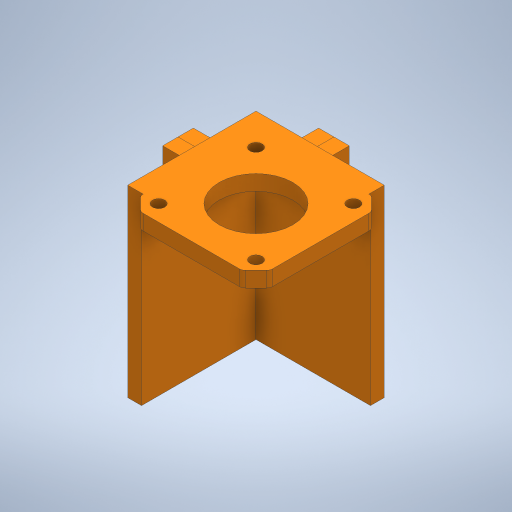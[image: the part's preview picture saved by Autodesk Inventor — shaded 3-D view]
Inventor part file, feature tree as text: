
AUTODESK INVENTOR PART (.ipt)
format: ipt  version: 2023 (Build 270158000, 158)  size: 452,608 bytes
history: native  units: mm
features: extrude x9, sketch x8, projected_geometry x4, other x3, fillet x1, reference x1
ambient origin geometry x8: Origin, YZ Plane, XZ Plane, XY Plane, X Axis, Y Axis, Z Axis, Center Point
bodies: Solid1 (feature_tree)
feature tree (26):
  extrude  "Extrusion1"  Depth=4.0mm
  extrude  "Extrusion3"  Depth=4.0mm
  extrude  "Extrusion4"  Depth=5.0mm TaperAngle=0.0deg
  extrude  "Extrusion9"  Depth=5.0mm
  extrude  "Extrusion7"  Depth=5.0mm TaperAngle=0.0deg
  extrude  "Extrusion10"  Depth=0.5mm
  extrude  "Extrusion11"  Depth=20.0mm TaperAngle=0.0deg
  extrude  "Extrusion12"  Depth=5.0mm
  fillet  "Fillet1"  Radius=4.5mm
  extrude  "Extrusion13"  Depth=0.5mm
  sketch  "Sketch1"  dims[d0=24.0mm d1=4.0mm]
  reference  "Reference1"
  sketch  "Sketch4"  dims[d2=4.0mm d3=4.0mm]
  projected_geometry  "Projected Loop1"
  sketch  "Sketch7"  dims[d4=4.0mm d5=5.0mm d6=0.0mm]
  sketch  "Sketch11"  dims[d11=5.0mm d12=5.0mm]
  sketch  "Sketch12"  dims[d15=40.0mm d16=0.0mm d17=5.0mm d18=0.0mm]
  sketch  "Sketch13"  dims[d35=0.5mm d36=0.5mm]
  sketch  "Sketch14"  dims[d37=35.0mm d38=0.0mm d52=20.0mm d53=0.0mm]
  projected_geometry  "Projected Loop2"
  sketch  "Sketch15"  dims[d54=5.0mm d55=5.0mm d56=4.5mm d57=0.5mm d58=20.0mm d59=0.0mm d60=10.0mm d61=10.0mm d62=5.0mm d63=5.0mm d64=20.0mm d65=10.0mm d66=20.0mm d67=0.0mm d68=10.0mm d69=10.0mm d70=20.0mm d71=10.0mm d72=5.0mm d73=5.0mm d74=40.0mm d75=0.0mm d76=5.0mm d77=8.0mm d78=8.0mm d79=5.0mm d80=5.0mm d81=20.0mm d82=20.0mm d83=0.0mm d84=0.0mm d85=20.0mm d86=0.0mm]
  projected_geometry  "Projected Loop3"
  projected_geometry  "Projected Loop4"
  other  "<userpath>\OneDrive\ClawdDrive\Objet3D\3DPrinter\inventor\3DPrinterBeltCoreXY.iam"
  other  "3DPrinterBeltCoreXY.iam"
  other  "E3D Stepper Motor:1"
